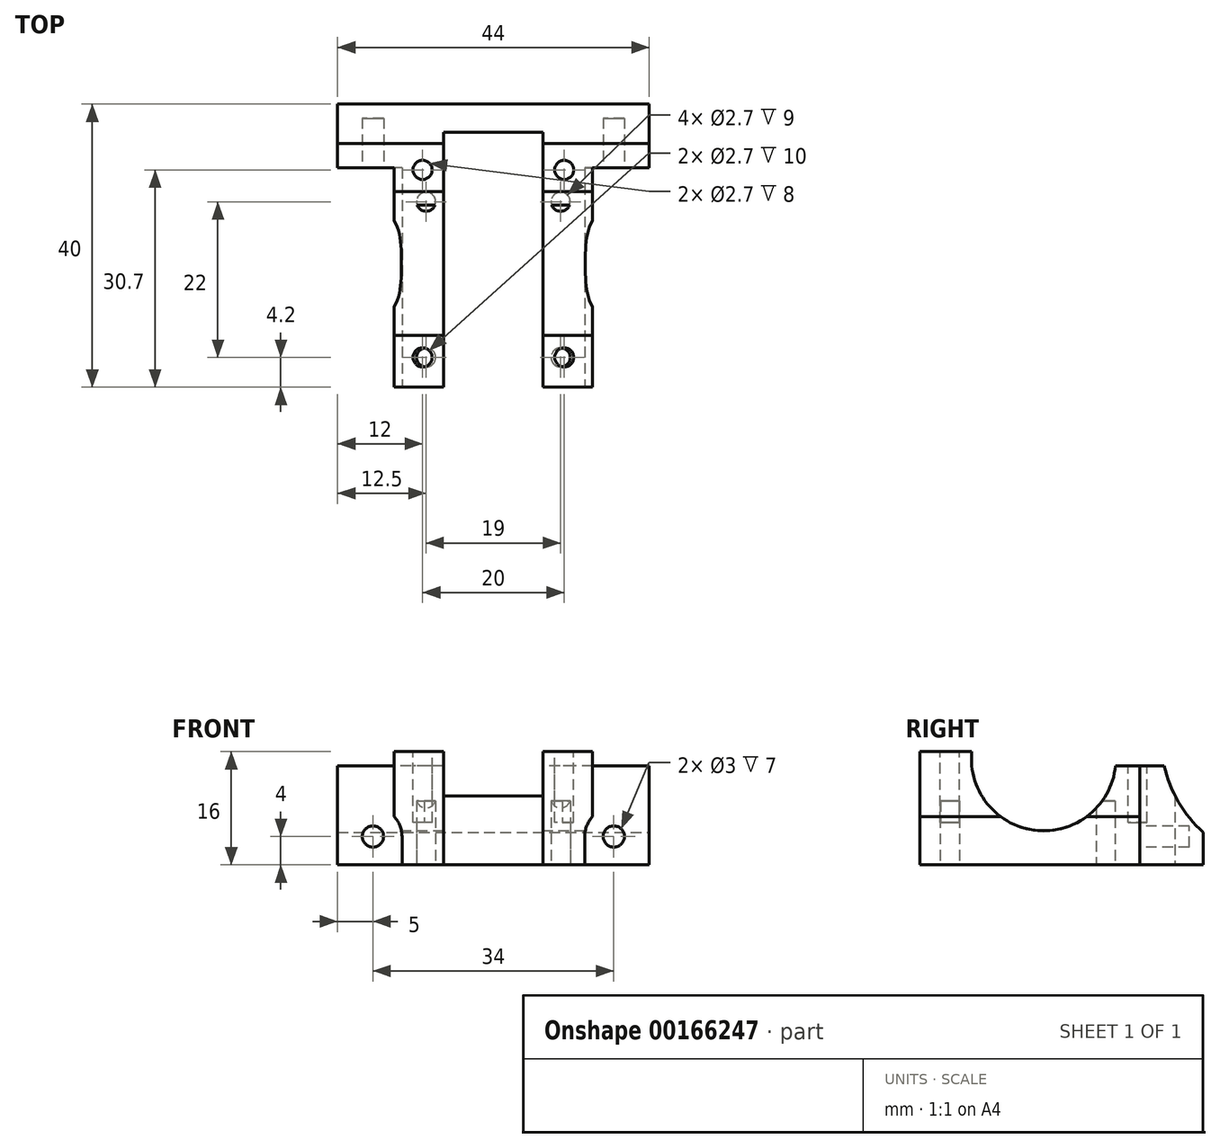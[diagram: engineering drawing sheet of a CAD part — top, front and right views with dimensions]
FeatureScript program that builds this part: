
annotation { "Feature Type Name" : "Feature", "Feature Type Description" : "" }
export const myFeature = defineFeature(function(context is Context, id is Id, definition is map)
    precondition{}
    {
        {
            var Q0;
            Q0=qCreatedBy(makeId("Top.planeOp"),FACE);
            var sketch = newSketch(context, id + "F0", { "sketchPlane" : qUnion([Q0])});
            skLineSegment(sketch, "E0.bottom", {"start": v(-14, 0) * mm, "end": v(-7, 0) * mm});
            skLineSegment(sketch, "E0.top", {"start": v(-14, 31) * mm, "end": v(-7, 31) * mm});
            skLineSegment(sketch, "E0.left", {"start": v(-14, 0) * mm, "end": v(-14, 31) * mm});
            skLineSegment(sketch, "E0.right", {"start": v(14, 0) * mm, "end": v(14, 31) * mm});
            skLineSegment(sketch, "E1", {"start": v(-14, 31) * mm, "end": v(-22, 31) * mm});
            skLineSegment(sketch, "E2", {"start": v(14, 31) * mm, "end": v(22, 31) * mm});
            skLineSegment(sketch, "E3", {"start": v(22, 40) * mm, "end": v(-22, 40) * mm});
            skLineSegment(sketch, "E4", {"start": v(-22, 40) * mm, "end": v(-22, 31) * mm});
            skLineSegment(sketch, "E5", {"start": v(22, 40) * mm, "end": v(22, 31) * mm});
            skLineSegment(sketch, "E6.left", {"start": v(-7, 31) * mm, "end": v(-7, 0) * mm});
            skLineSegment(sketch, "E6.right", {"start": v(7, 31) * mm, "end": v(7, 0) * mm});
            skLineSegment(sketch, "E7.trimOffspring", {"start": v(7, 0) * mm, "end": v(14, 0) * mm});
            skLineSegment(sketch, "E8", {"start": v(-7, 31) * mm, "end": v(-7, 36) * mm});
            skLineSegment(sketch, "E9", {"start": v(-7, 36) * mm, "end": v(7, 36) * mm});
            skLineSegment(sketch, "E10", {"start": v(7, 31) * mm, "end": v(7, 36) * mm});
            skLineSegment(sketch, "E11.trimOffspring", {"start": v(7, 31) * mm, "end": v(14, 31) * mm});
            skSolve(sketch);
        }
        {
            var Q0;
            Q0=qSketchRegion(id+"F0",true);
            extrude(context, id + "F1", {"entities" : qUnion([Q0]), "depth" : 14 * mm});
        }
        {
            var Q0;
            Q0=makeQuery(id+"F1.opExtrude","CAP_FACE",FACE,{"disambiguationData":[OSD([sQuery(id+"F0.wireOp",EDGE,"E0.bottom"),sQuery(id+"F0.wireOp",EDGE,"E0.top"),sQuery(id+"F0.wireOp",EDGE,"E0.left"),sQuery(id+"F0.wireOp",EDGE,"E0.right"),sQuery(id+"F0.wireOp",EDGE,"E1"),sQuery(id+"F0.wireOp",EDGE,"E2"),sQuery(id+"F0.wireOp",EDGE,"E3"),sQuery(id+"F0.wireOp",EDGE,"E4"),sQuery(id+"F0.wireOp",EDGE,"E5"),sQuery(id+"F0.wireOp",EDGE,"E6.left"),sQuery(id+"F0.wireOp",EDGE,"E6.right"),sQuery(id+"F0.wireOp",EDGE,"E7.trimOffspring")])],"isStart":false});
            var sketch = newSketch(context, id + "F2", { "sketchPlane" : qUnion([Q0])});
            skCircle(sketch, "E12", {"center": v(-10, 4.2) * mm, "radius": 1.35 * mm});
            skCircle(sketch, "E13", {"center": v(-10, 30.7) * mm, "radius": 1.35 * mm});
            skCircle(sketch, "E14", {"center": v(10, 30.7) * mm, "radius": 1.35 * mm});
            skCircle(sketch, "E15", {"center": v(10, 4.2) * mm, "radius": 1.35 * mm});
            skSolve(sketch);
        }
        {
            var Q0;
            Q0=qSketchRegion(id+"F2",true);
            extrude(context, id + "F3", {"entities" : qUnion([Q0]), "operationType" : NewBodyOperationType.REMOVE, "oppositeDirection" : true, "depth" : 8 * mm});
        }
        {
            var Q0;
            Q0=makeQuery(id+"F1.opExtrude","SWEPT_FACE",FACE,{"disambiguationData":[OSD([sQuery(id+"F0.wireOp",EDGE,"E0.left")])]});
            var sketch = newSketch(context, id + "F4", { "sketchPlane" : qUnion([Q0])});
            skCircle(sketch, "E16", {"center": v(-17.45, 15) * mm, "radius": 10.2 * mm});
            skSolve(sketch);
        }
        {
            var Q0;
            Q0=qSketchRegion(id+"F4",true);
            extrude(context, id + "F5", {"entities" : qUnion([Q0]), "operationType" : NewBodyOperationType.REMOVE, "oppositeDirection" : true, "depth" : 30 * mm});
        }
        {
            var Q0;
            Q0=makeQuery(id+"F1.opExtrude","CAP_FACE",FACE,{"disambiguationData":[OSD([sQuery(id+"F0.wireOp",EDGE,"E0.bottom"),sQuery(id+"F0.wireOp",EDGE,"E0.top"),sQuery(id+"F0.wireOp",EDGE,"E0.left"),sQuery(id+"F0.wireOp",EDGE,"E0.right"),sQuery(id+"F0.wireOp",EDGE,"E1"),sQuery(id+"F0.wireOp",EDGE,"E2"),sQuery(id+"F0.wireOp",EDGE,"E3"),sQuery(id+"F0.wireOp",EDGE,"E4"),sQuery(id+"F0.wireOp",EDGE,"E5"),sQuery(id+"F0.wireOp",EDGE,"E6.left"),sQuery(id+"F0.wireOp",EDGE,"E6.right"),sQuery(id+"F0.wireOp",EDGE,"E7.trimOffspring")])],"isStart":true});
            var sketch = newSketch(context, id + "F6", { "sketchPlane" : qUnion([Q0])});
            skCircle(sketch, "E17", {"center": v(9.5, -4.2) * mm, "radius": 1.35 * mm});
            skCircle(sketch, "E18", {"center": v(-9.5, -4.2) * mm, "radius": 1.35 * mm});
            skCircle(sketch, "E19", {"center": v(9.5, -26.2) * mm, "radius": 1.35 * mm});
            skCircle(sketch, "E20", {"center": v(-9.5, -26.2) * mm, "radius": 1.35 * mm});
            skSolve(sketch);
        }
        {
            var Q0;
            Q0=qSketchRegion(id+"F6",true);
            extrude(context, id + "F7", {"entities" : qUnion([Q0]), "operationType" : NewBodyOperationType.REMOVE, "oppositeDirection" : true, "depth" : 9 * mm});
        }
        {
            var Q0;
            Q0=makeQuery(id+"F1.opExtrude","SWEPT_FACE",FACE,{"disambiguationData":[OSD([sQuery(id+"F0.wireOp",EDGE,"E2")])]});
            var sketch = newSketch(context, id + "F8", { "sketchPlane" : qUnion([Q0])});
            skCircle(sketch, "E21", {"center": v(-17, 4) * mm, "radius": 1.5 * mm});
            skCircle(sketch, "E22", {"center": v(17, 4) * mm, "radius": 1.5 * mm});
            skSolve(sketch);
        }
        {
            var Q0;
            Q0=qSketchRegion(id+"F8",true);
            extrude(context, id + "F9", {"entities" : qUnion([Q0]), "operationType" : NewBodyOperationType.REMOVE, "oppositeDirection" : true, "depth" : 7 * mm});
        }
        {
            var Q0;
            Q0=makeQuery(id+"F1.opExtrude","SWEPT_FACE",FACE,{"disambiguationData":[OSD([sQuery(id+"F0.wireOp",EDGE,"E5")])]});
            var sketch = newSketch(context, id + "F10", { "sketchPlane" : qUnion([Q0])});
            skCircle(sketch, "E23", {"center": v(52, 18) * mm, "radius": 18 * mm});
            skSolve(sketch);
        }
        {
            var Q0;
            Q0=qSketchRegion(id+"F10",true);
            extrude(context, id + "F11", {"entities" : qUnion([Q0]), "operationType" : NewBodyOperationType.REMOVE, "endBound" : BoundingType.THROUGH_ALL, "oppositeDirection" : true, "depth" : 25 * mm});
        }
        {
            var Q0;
            Q0=makeQuery(id+"F1.opExtrude","SWEPT_FACE",FACE,{"disambiguationData":[OSD([sQuery(id+"F0.wireOp",EDGE,"E7.trimOffspring")])]});
            var sketch = newSketch(context, id + "F12", { "sketchPlane" : qUnion([Q0])});
            skArc(sketch, "E24", {"start": v(-12.9, 4) * mm, "mid": v(-18.7, 7.73) * mm, "end": v(-19.7, 0.92) * mm});
            skArc(sketch, "E25", {"start": v(19.7, 0.92) * mm, "mid": v(18.7, 7.73) * mm, "end": v(12.9, 4) * mm});
            skLineSegment(sketch, "E26", {"start": v(-12.9, 4) * mm, "end": v(-12.9, -5.05) * mm});
            skLineSegment(sketch, "E27", {"start": v(12.9, 4) * mm, "end": v(12.9, -5.05) * mm});
            skLineSegment(sketch, "E28", {"start": v(-12.9, -5.05) * mm, "end": v(-19.7, 0.92) * mm});
            skLineSegment(sketch, "E29", {"start": v(12.9, -5.05) * mm, "end": v(19.7, 0.92) * mm});
            skSolve(sketch);
        }
        {
            var Q0;
            Q0=qSketchRegion(id+"F12",true);
            var Q1;
            Q1=makeQuery(id+"F1.opExtrude","SWEPT_FACE",FACE,{"disambiguationData":[OSD([sQuery(id+"F0.wireOp",EDGE,"E1")])]});
            extrude(context, id + "F13", {"entities" : qUnion([Q0]), "operationType" : NewBodyOperationType.REMOVE, "endBound" : BoundingType.UP_TO_SURFACE, "oppositeDirection" : true, "endBoundEntityFace" : qUnion([Q1]), "depth" : 25 * mm});
        }
        {
            var Q0;
            {var subQ0=sQuery(id+"F0.wireOp",EDGE,"E7.trimOffspring");var subQ1=sQuery(id+"F0.wireOp",EDGE,"E10");var subQ2=sQuery(id+"F0.wireOp",EDGE,"E6.right");var subQ3=sQuery(id+"F0.wireOp",EDGE,"E0.right");Q0=makeQuery(id+"F5.boolean.opBoolean","SPLIT",FACE,{"disambiguationData":[TD([makeQuery(id+"F1.opExtrude","SWEPT_FACE",FACE,{"disambiguationData":[OSD([subQ0])]})])],"derivedFrom":makeQuery(id+"F1.opExtrude","CAP_FACE",FACE,{"disambiguationData":[OSD([sQuery(id+"F0.wireOp",EDGE,"E0.bottom"),sQuery(id+"F0.wireOp",EDGE,"E0.left"),subQ3,sQuery(id+"F0.wireOp",EDGE,"E1"),sQuery(id+"F0.wireOp",EDGE,"E2"),sQuery(id+"F0.wireOp",EDGE,"E3"),sQuery(id+"F0.wireOp",EDGE,"E4"),sQuery(id+"F0.wireOp",EDGE,"E5"),sQuery(id+"F0.wireOp",EDGE,"E6.left"),subQ2,subQ0,sQuery(id+"F0.wireOp",EDGE,"E8"),sQuery(id+"F0.wireOp",EDGE,"E9"),subQ1])],"isStart":false})});}
            var sketch = newSketch(context, id + "F14", { "sketchPlane" : qUnion([Q0])});
            skCircle(sketch, "E30.0", {"center": v(10, 4.2) * mm, "radius": 1.35 * mm});
            skLineSegment(sketch, "E31.0", {"start": v(14, 0) * mm, "end": v(14, 7.3) * mm});
            skLineSegment(sketch, "E32.0", {"start": v(7, 0) * mm, "end": v(14, 0) * mm});
            skLineSegment(sketch, "E33.0", {"start": v(7, 7.3) * mm, "end": v(7, 0) * mm});
            skLineSegment(sketch, "E34.0", {"start": v(7, 7.3) * mm, "end": v(14, 7.3) * mm});
            skLineSegment(sketch, "E35.0", {"start": v(-7, 7.3) * mm, "end": v(-7, 0) * mm});
            skLineSegment(sketch, "E36.0.0", {"start": v(-14, 7.3) * mm, "end": v(-7, 7.3) * mm});
            skLineSegment(sketch, "E36.0.1", {"start": v(-14, 7.3) * mm, "end": v(-14, 0) * mm});
            skLineSegment(sketch, "E36.0.2", {"start": v(-14, 0) * mm, "end": v(-7, 0) * mm});
            skLineSegment(sketch, "E36.0.3", {"start": v(-7, 0) * mm, "end": v(-7, 7.3) * mm});
            skCircle(sketch, "E37.0", {"center": v(-10, 4.2) * mm, "radius": 1.35 * mm});
            skSolve(sketch);
        }
        {
            var Q0;
            Q0=qSketchRegion(id+"F14",true);
            extrude(context, id + "F15", {"entities" : qUnion([Q0]), "operationType" : NewBodyOperationType.ADD, "depth" : 2 * mm});
        }
    });
